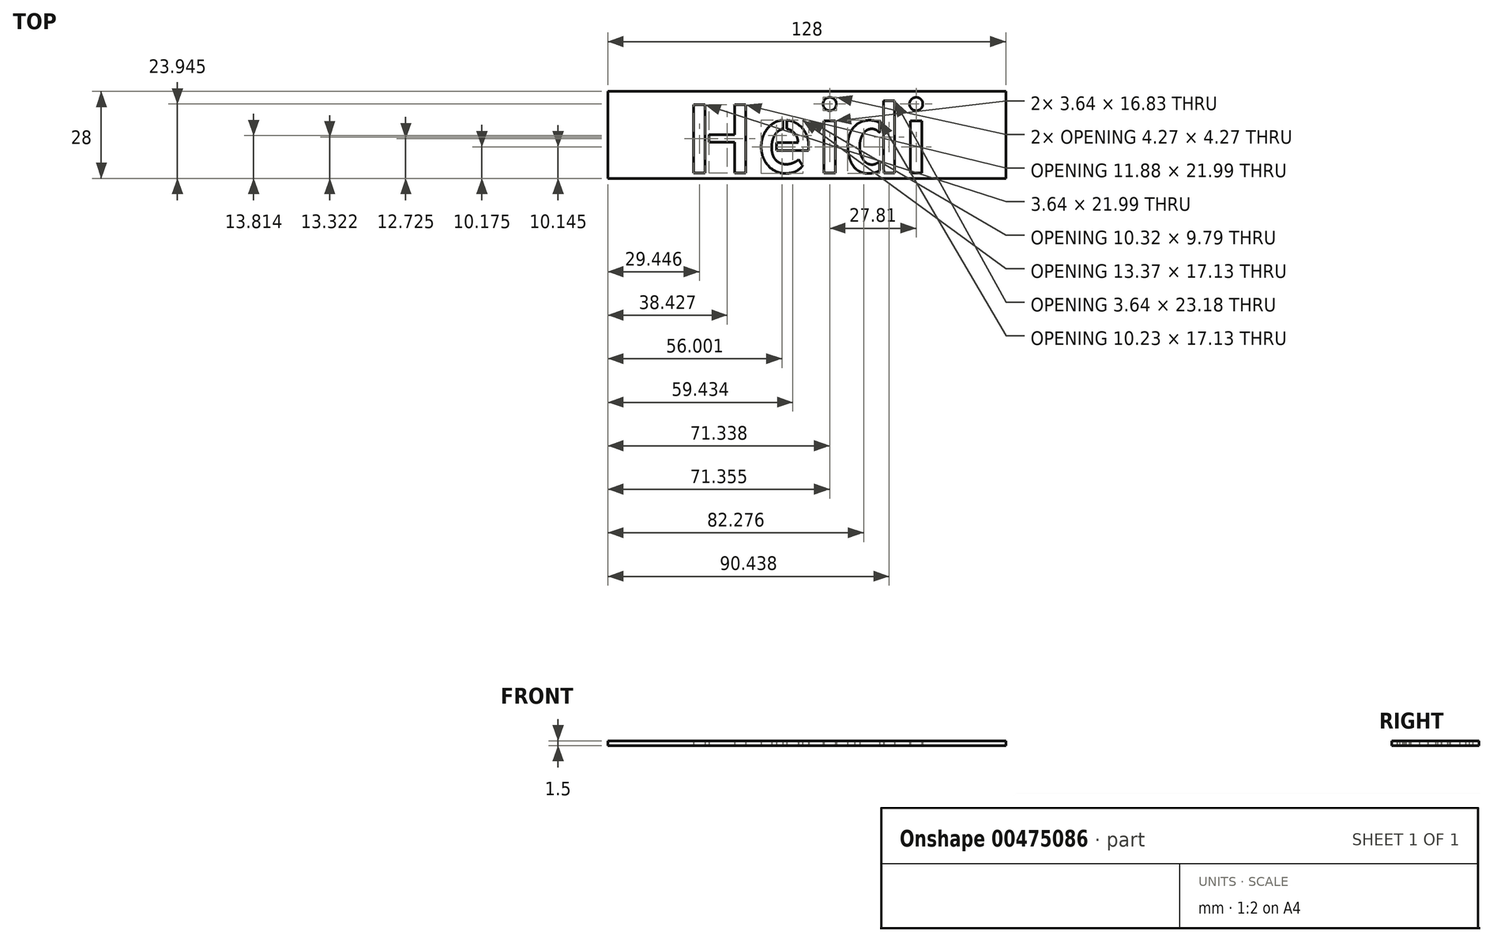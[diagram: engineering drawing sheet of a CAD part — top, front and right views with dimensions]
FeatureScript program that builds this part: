
annotation { "Feature Type Name" : "Feature", "Feature Type Description" : "" }
export const myFeature = defineFeature(function(context is Context, id is Id, definition is map)
    precondition{}
    {
        {
            var Q0;
            Q0=qCreatedBy(makeId("Top.planeOp"),FACE);
            var sketch = newSketch(context, id + "F0", { "sketchPlane" : qUnion([Q0])});
            skLineSegment(sketch, "E0.bottom", {"start": v(64, -14) * mm, "end": v(-64, -14) * mm});
            skLineSegment(sketch, "E0.top", {"start": v(64, 14) * mm, "end": v(-64, 14) * mm});
            skLineSegment(sketch, "E0.left", {"start": v(64, -14) * mm, "end": v(64, 14) * mm});
            skLineSegment(sketch, "E0.right", {"start": v(-64, -14) * mm, "end": v(-64, 14) * mm});
            skPoint(sketch, "E0.middle", {"position": v(0, 0) * mm});
            skText(sketch, "E1", { "text": "Heidi", "fontName": "AllertaStencil-Regular.ttf"});
            const initialGuessF0  = {"E1": [-0.03918, -0.01227, 1, 0, 0.022]};
            skSetInitialGuess(sketch, initialGuessF0);
            skSolve(sketch);
        }
        {
            var Q0;
            Q0=makeQuery(id+"F0.imprint","IMPRINT",FACE,{"disambiguationData":[TD([[makeQuery(id+"F0.imprint","IMPRINT",EDGE,{"derivedFrom":sQuery(id+"F0.wireOp",EDGE,"E0.bottom")}),-1.0]])]});
            extrude(context, id + "F1", {"entities" : qUnion([Q0]), "depth" : 1.5 * mm});
        }
    });
